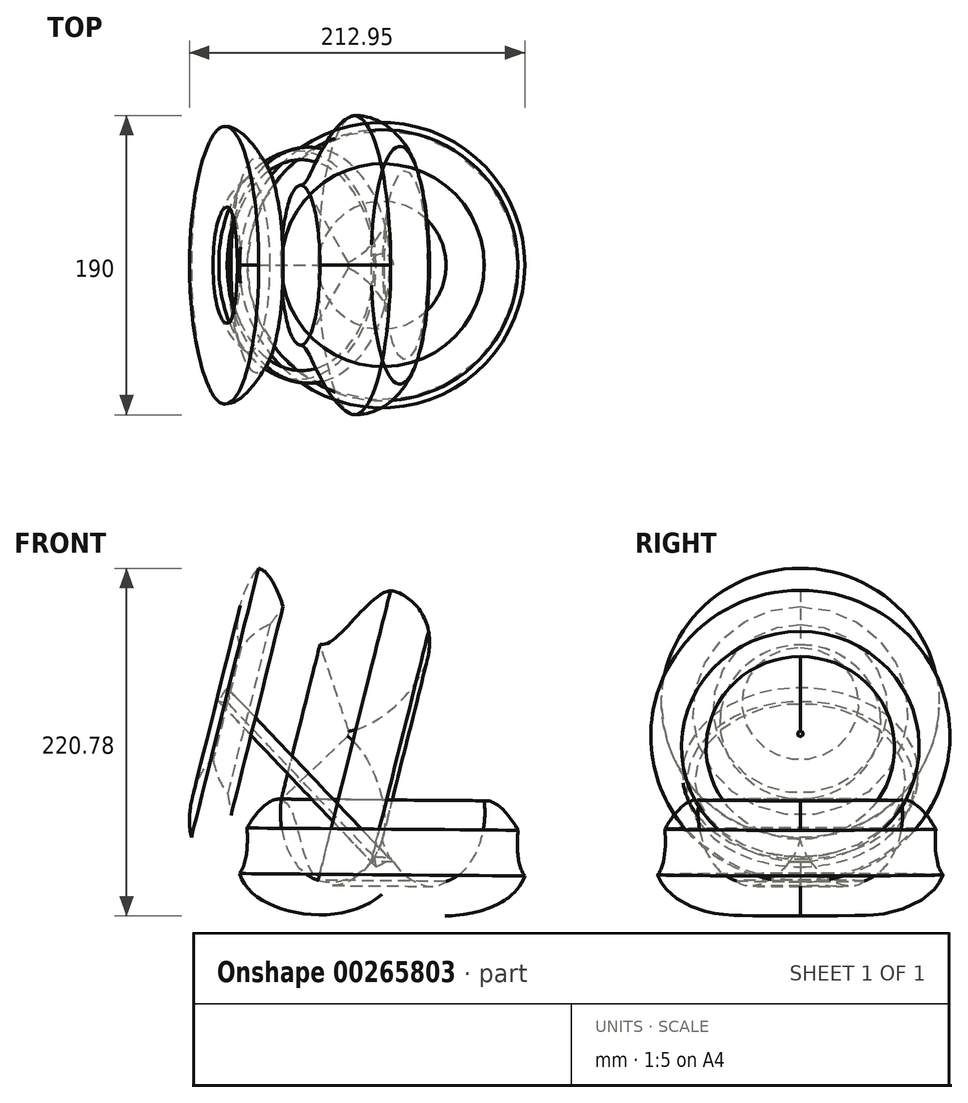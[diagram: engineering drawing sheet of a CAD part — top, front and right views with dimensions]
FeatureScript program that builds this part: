
annotation { "Feature Type Name" : "Feature", "Feature Type Description" : "" }
export const myFeature = defineFeature(function(context is Context, id is Id, definition is map)
    precondition{}
    {
        {
            var Q0;
            Q0=qCreatedBy(makeId("Front.planeOp"),FACE);
            var sketch = newSketch(context, id + "F0", { "sketchPlane" : qUnion([Q0])});
            skFitSpline(sketch, "E0", {"points": [v(-65.97, 59.97) * mm, v(-65.11, -31.13) * mm, v(26.56, 36.84) * mm, v(56.26, -32.27) * mm, v(15.42, -58.26) * mm, v(-8, -6.85) * mm, v(-34.55, -53.97) * mm, v(55.97, -67.1) * mm, v(60.83, 58.54) * mm, v(20.56, 60.54) * mm, v(-45.12, 19.13) * mm, v(-42.26, 63.97) * mm, v(-65.97, 59.97) * mm]});
            skFitSpline(sketch, "E1", {"points": [v(-8, -6.85) * mm, v(26.56, 36.84) * mm, v(56.26, -32.27) * mm, v(15.42, -58.26) * mm, v(-8, -6.85) * mm]});
            skFitSpline(sketch, "E2", {"points": [v(-65.11, -31.13) * mm, v(-34.55, -53.97) * mm, v(-45.12, 19.13) * mm, v(-65.11, -31.13) * mm]});
            skFitSpline(sketch, "E3", {"points": [v(-42.26, 63.97) * mm, v(20.56, 60.54) * mm, v(-31.81, -9) * mm, v(-42.26, 63.97) * mm]});
            skLineSegment(sketch, "E4", {"start": v(-65.97, 59.97) * mm, "end": v(26.56, 36.84) * mm});
            skLineSegment(sketch, "E5", {"start": v(60.83, 58.54) * mm, "end": v(-8, -6.85) * mm});
            skLineSegment(sketch, "E6", {"start": v(56.26, -32.27) * mm, "end": v(55.97, -67.1) * mm});
            skLineSegment(sketch, "E7", {"start": v(-34.55, -53.97) * mm, "end": v(-45.12, 19.13) * mm});
            skSolve(sketch);
        }
        {
            var Q0;
            {var subQ0=sQuery(id+"F0.wireOp",EDGE,"E2");var subQ1=sQuery(id+"F0.wireOp",EDGE,"E0");var subQ2=makeQuery(id+"F0.imprint","INTERSECT",VERTEX,{"disambiguationData":[OD(0.0)],"derivedFrom":[subQ1,subQ0]});Q0=makeQuery(id+"F0.imprint","IMPRINT",FACE,{"disambiguationData":[TD([[makeQuery(id+"F0.imprint","IMPRINT",EDGE,{"disambiguationData":[TD([[subQ2,-1.0]])],"derivedFrom":subQ1}),1.0]])]});}
            var Q1;
            Q1=sQuery(id+"F0.wireOp",EDGE,"E4");
            revolve(context, id + "F1", {"entities" : qUnion([Q0]), "axis" : qUnion([Q1]), "revolveType" : RevolveType.FULL});
        }
        {
            var Q0;
            {var subQ0=sQuery(id+"F0.wireOp",EDGE,"E6");Q0=makeQuery(id+"F0.imprint","IMPRINT",FACE,{"disambiguationData":[TD([[makeQuery(id+"F0.imprint","IMPRINT",EDGE,{"derivedFrom":subQ0}),-1.0]])]});}
            var Q1;
            Q1=sQuery(id+"F0.wireOp",EDGE,"E6");
            revolve(context, id + "F2", {"entities" : qUnion([Q0]), "axis" : qUnion([Q1]), "revolveType" : RevolveType.FULL});
        }
        {
            var Q0;
            {var subQ0=sQuery(id+"F0.wireOp",EDGE,"E1");var subQ1=sQuery(id+"F0.wireOp",EDGE,"E0");var subQ2=makeQuery(id+"F0.imprint","INTERSECT",VERTEX,{"disambiguationData":[OD(1.0)],"derivedFrom":[subQ1,subQ0]});Q0=makeQuery(id+"F0.imprint","IMPRINT",FACE,{"disambiguationData":[TD([[makeQuery(id+"F0.imprint","IMPRINT",EDGE,{"disambiguationData":[TD([[subQ2,-1.0]])],"derivedFrom":subQ0}),-1.0]])]});}
            var Q1;
            Q1=sQuery(id+"F0.wireOp",EDGE,"E4");
            revolve(context, id + "F3", {"entities" : qUnion([Q0]), "axis" : qUnion([Q1]), "revolveType" : RevolveType.FULL});
        }
        {
            var Q0;
            {var subQ0=sQuery(id+"F0.wireOp",EDGE,"E4");var subQ1=sQuery(id+"F0.wireOp",EDGE,"E0");var subQ2=makeQuery(id+"F0.imprint","INTERSECT",VERTEX,{"disambiguationData":[OD(0.0)],"derivedFrom":[subQ1,subQ0]});Q0=makeQuery(id+"F0.imprint","IMPRINT",FACE,{"disambiguationData":[TD([[makeQuery(id+"F0.imprint","IMPRINT",EDGE,{"disambiguationData":[TD([[subQ2,-1.0]])],"derivedFrom":subQ1}),1.0]])]});}
            var Q1;
            Q1=sQuery(id+"F0.wireOp",EDGE,"E5");
            revolve(context, id + "F4", {"entities" : qUnion([Q0]), "axis" : qUnion([Q1]), "revolveType" : RevolveType.FULL});
        }
    });
